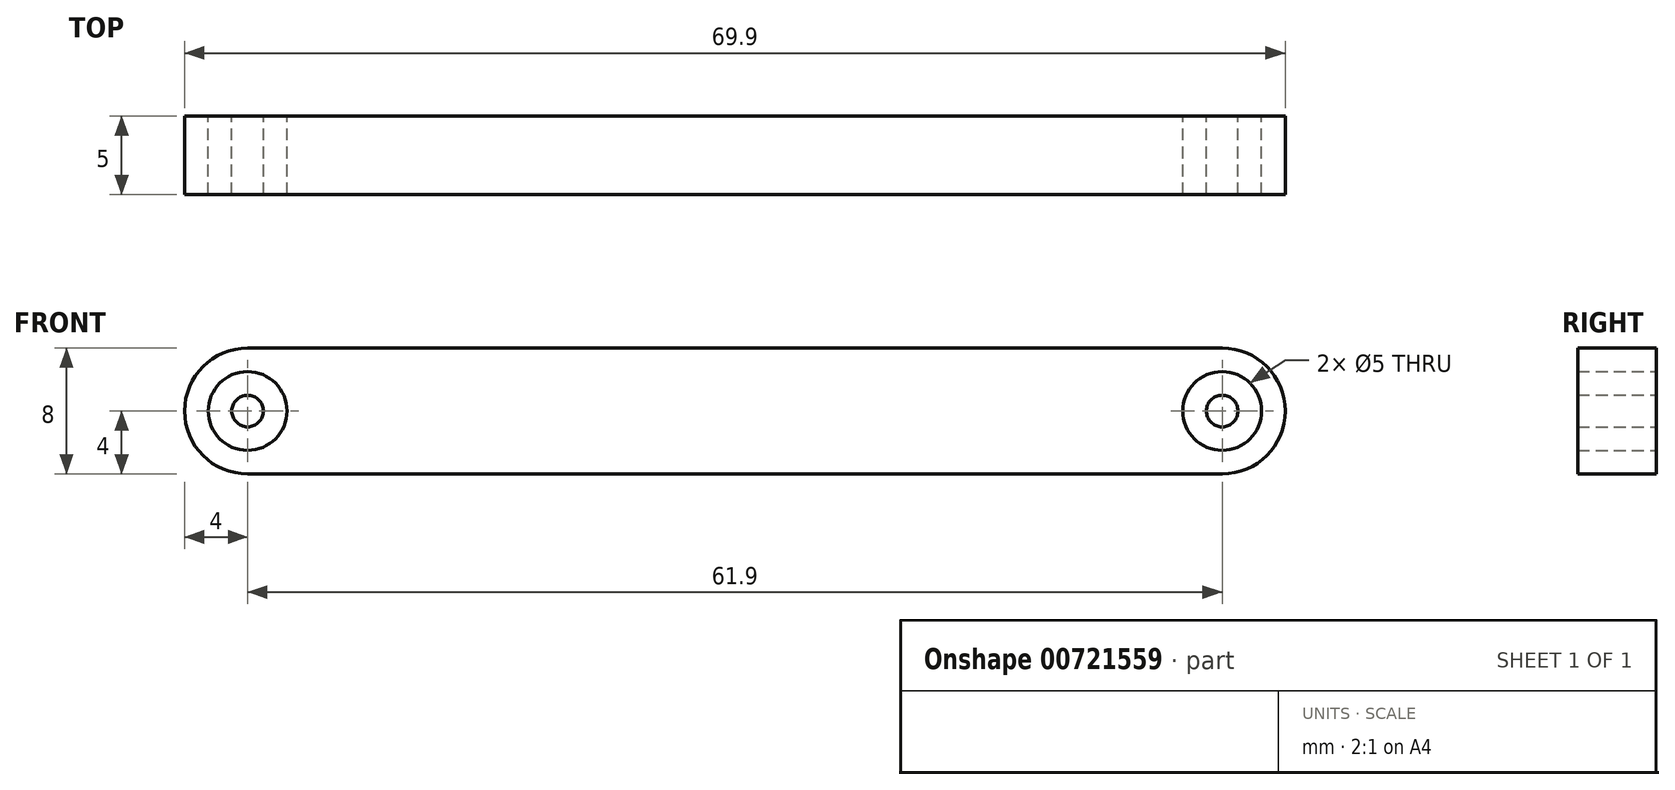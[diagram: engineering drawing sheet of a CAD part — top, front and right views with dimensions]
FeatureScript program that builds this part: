
annotation { "Feature Type Name" : "Feature", "Feature Type Description" : "" }
export const myFeature = defineFeature(function(context is Context, id is Id, definition is map)
    precondition{}
    {
        {
            var Q0;
            Q0=qCreatedBy(makeId("Front.planeOp"),FACE);
            var sketch = newSketch(context, id + "F0", { "sketchPlane" : qUnion([Q0])});
            skLineSegment(sketch, "E0.bottom", {"start": v(30.95, 4) * mm, "end": v(-30.95, 4) * mm});
            skLineSegment(sketch, "E0.top", {"start": v(30.95, -4) * mm, "end": v(-30.95, -4) * mm});
            skPoint(sketch, "E0.middle", {"position": v(0, 0) * mm});
            skArc(sketch, "E1", {"start": v(30.95, -4) * mm, "mid": v(34.95, 0) * mm, "end": v(30.95, 4) * mm});
            skArc(sketch, "E2", {"start": v(-30.95, 4) * mm, "mid": v(-34.95, 0) * mm, "end": v(-30.95, -4) * mm});
            skCircle(sketch, "E3", {"center": v(-30.95, 0) * mm, "radius": 1 * mm});
            skCircle(sketch, "E4", {"center": v(30.95, 0) * mm, "radius": 2.5 * mm});
            skCircle(sketch, "E5", {"center": v(-30.95, 0) * mm, "radius": 2.5 * mm});
            skCircle(sketch, "E6", {"center": v(30.95, 0) * mm, "radius": 1 * mm});
            skSolve(sketch);
        }
        {
            var Q0;
            Q0=makeQuery(id+"F0.imprint","IMPRINT",FACE,{"disambiguationData":[TD([[makeQuery(id+"F0.imprint","IMPRINT",EDGE,{"derivedFrom":sQuery(id+"F0.wireOp",EDGE,"E0.bottom")}),1.0]])]});
            var Q1;
            Q1=makeQuery(id+"F0.imprint","IMPRINT",FACE,{"disambiguationData":[TD([[makeQuery(id+"F0.imprint","IMPRINT",EDGE,{"derivedFrom":sQuery(id+"F0.wireOp",EDGE,"E3")}),1.0]])]});
            var Q2;
            Q2=makeQuery(id+"F0.imprint","IMPRINT",FACE,{"disambiguationData":[TD([[makeQuery(id+"F0.imprint","IMPRINT",EDGE,{"derivedFrom":sQuery(id+"F0.wireOp",EDGE,"E6")}),1.0]])]});
            extrude(context, id + "F1", {"entities" : qUnion([Q0, Q1, Q2]), "endBound" : BoundingType.SYMMETRIC, "depth" : 5 * mm, "offsetDistance" : 25.4 * mm});
        }
    });
